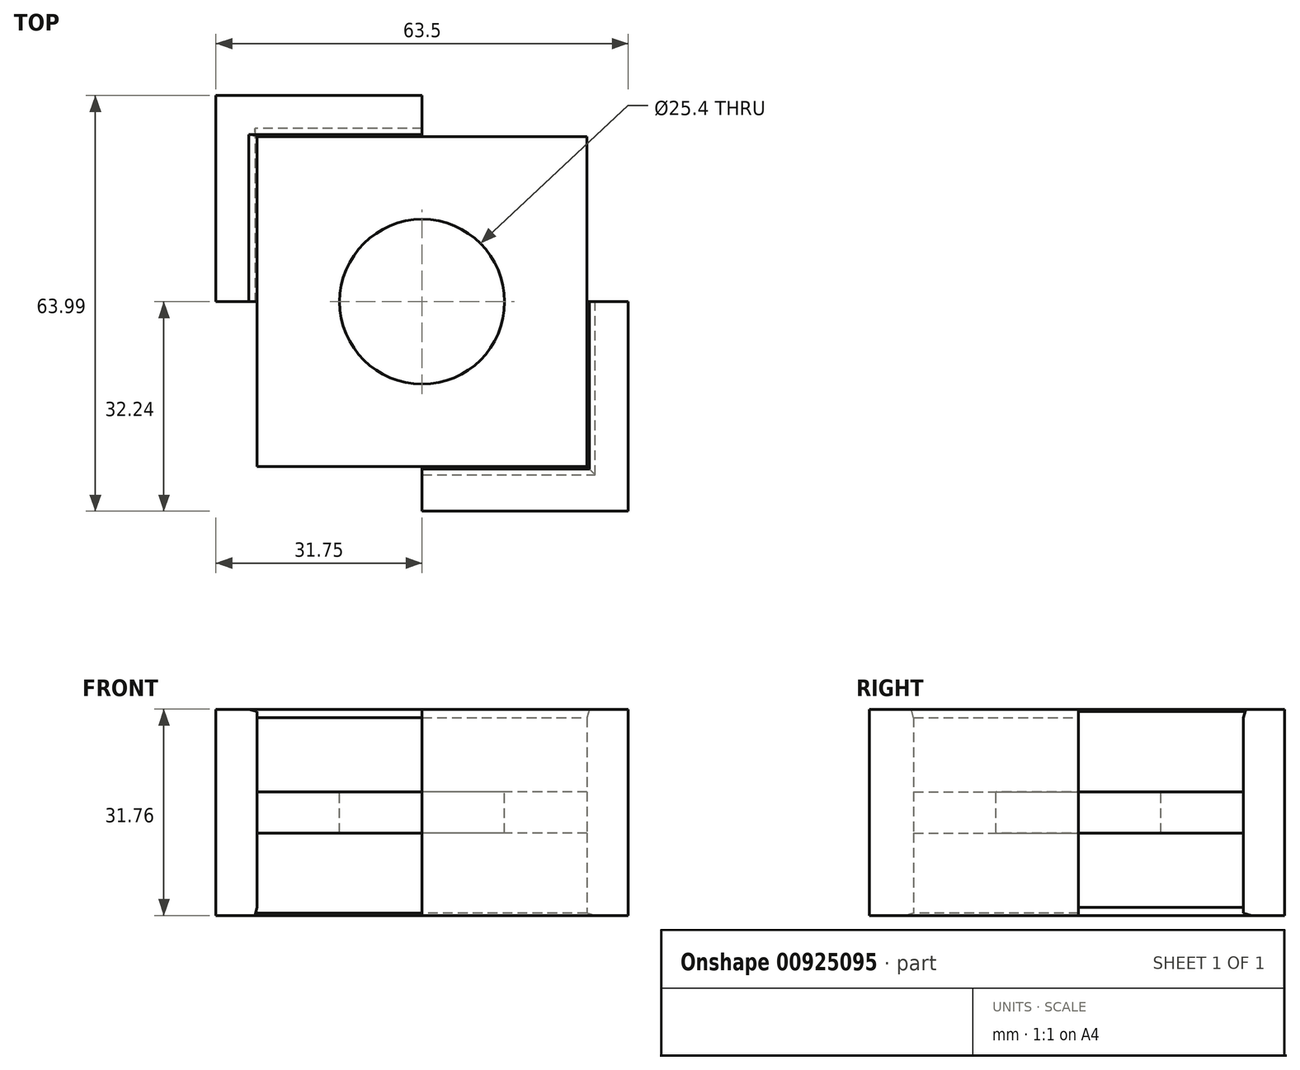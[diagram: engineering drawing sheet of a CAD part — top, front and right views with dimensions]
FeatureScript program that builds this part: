
annotation { "Feature Type Name" : "Feature", "Feature Type Description" : "" }
export const myFeature = defineFeature(function(context is Context, id is Id, definition is map)
    precondition{}
    {
        {
            var Q0;
            Q0=qCreatedBy(makeId("Top.planeOp"),FACE);
            var sketch = newSketch(context, id + "F0", { "sketchPlane" : qUnion([Q0])});
            skLineSegment(sketch, "E0.bottom", {"start": v(0, 0) * mm, "end": v(-50.8, 0) * mm});
            skLineSegment(sketch, "E0.top", {"start": v(0, 50.8) * mm, "end": v(-50.8, 50.8) * mm});
            skLineSegment(sketch, "E0.left", {"start": v(0, 0) * mm, "end": v(0, 50.8) * mm});
            skLineSegment(sketch, "E0.right", {"start": v(-50.8, 0) * mm, "end": v(-50.8, 50.8) * mm});
            skSolve(sketch);
        }
        {
            var Q0;
            Q0=qCreatedBy(makeId("Top.planeOp"),FACE);
            var sketch = newSketch(context, id + "F1", { "sketchPlane" : qUnion([Q0])});
            skLineSegment(sketch, "E1", {"start": v(0, 0) * mm, "end": v(0, 25.4) * mm});
            skLineSegment(sketch, "E2", {"start": v(0, 25.4) * mm, "end": v(6.35, 25.4) * mm});
            skLineSegment(sketch, "E3", {"start": v(6.35, 25.4) * mm, "end": v(6.35, -6.84) * mm});
            skLineSegment(sketch, "E4", {"start": v(6.35, -6.84) * mm, "end": v(-25.4, -6.84) * mm});
            skLineSegment(sketch, "E5", {"start": v(-25.4, -6.84) * mm, "end": v(-25.4, 0) * mm});
            skLineSegment(sketch, "E6", {"start": v(-25.4, 0) * mm, "end": v(0, 0) * mm});
            skSolve(sketch);
        }
        {
            var Q0;
            Q0=qCreatedBy(makeId("Top.planeOp"),FACE);
            var sketch = newSketch(context, id + "F2", { "sketchPlane" : qUnion([Q0])});
            skLineSegment(sketch, "E7.0", {"start": v(-25.4, 50.8) * mm, "end": v(-50.8, 50.8) * mm});
            skLineSegment(sketch, "E8.0", {"start": v(-50.8, 25.4) * mm, "end": v(-50.8, 50.8) * mm});
            skLineSegment(sketch, "E9", {"start": v(-25.4, 57.15) * mm, "end": v(-57.15, 57.15) * mm});
            skLineSegment(sketch, "E10", {"start": v(-57.15, 57.15) * mm, "end": v(-57.15, 25.4) * mm});
            skLineSegment(sketch, "E11", {"start": v(-57.15, 25.4) * mm, "end": v(-50.8, 25.4) * mm});
            skLineSegment(sketch, "E12", {"start": v(-25.4, 57.15) * mm, "end": v(-25.4, 50.8) * mm});
            skPoint(sketch, "E13.orphan", {"position": v(0, 50.8) * mm});
            skPoint(sketch, "E14.orphan", {"position": v(-50.8, 0) * mm});
            skSolve(sketch);
        }
        {
            var Q0;
            Q0 = qSketchRegion(id + "F0", true);
            extrude(context, id + "F3", {"entities" : qUnion([Q0]), "endBound" : BoundingType.SYMMETRIC, "depth" : 6.35 * mm, "offsetDistance" : 25.4 * mm});
        }
        {
            var Q0;
            Q0 = qSketchRegion(id + "F1", true);
            extrude(context, id + "F4", {"entities" : qUnion([Q0]), "operationType" : NewBodyOperationType.ADD, "endBound" : BoundingType.SYMMETRIC, "depth" : 31.75 * mm, "offsetDistance" : 25.4 * mm});
        }
        {
            var Q0;
            Q0 = qSketchRegion(id + "F2", true);
            extrude(context, id + "F5", {"entities" : qUnion([Q0]), "operationType" : NewBodyOperationType.ADD, "endBound" : BoundingType.SYMMETRIC, "depth" : 31.75 * mm, "offsetDistance" : 25.4 * mm});
        }
        {
            var Q0;
            Q0=makeQuery(id+"F4.opExtrude","CAP_EDGE",EDGE,{"disambiguationData":[OSD([sQuery(id+"F1.wireOp",EDGE,"E6")])],"isStart":false});
            var Q1;
            Q1=makeQuery(id+"F4.opExtrude","CAP_EDGE",EDGE,{"disambiguationData":[OSD([sQuery(id+"F1.wireOp",EDGE,"E1")])],"isStart":false});
            var Q2;
            Q2=makeQuery(id+"F5.opExtrude","CAP_EDGE",EDGE,{"disambiguationData":[OSD([sQuery(id+"F2.wireOp",EDGE,"E7.0")])],"isStart":false});
            var Q3;
            Q3=makeQuery(id+"F5.opExtrude","CAP_EDGE",EDGE,{"disambiguationData":[OSD([sQuery(id+"F2.wireOp",EDGE,"E8.0")])],"isStart":false});
            var Q4;
            Q4=makeQuery(id+"F4.opExtrude","CAP_EDGE",EDGE,{"disambiguationData":[OSD([sQuery(id+"F1.wireOp",EDGE,"E6")])],"isStart":true});
            var Q5;
            Q5=makeQuery(id+"F4.opExtrude","CAP_EDGE",EDGE,{"disambiguationData":[OSD([sQuery(id+"F1.wireOp",EDGE,"E1")])],"isStart":true});
            var Q6;
            Q6=makeQuery(id+"F5.opExtrude","CAP_EDGE",EDGE,{"disambiguationData":[OSD([sQuery(id+"F2.wireOp",EDGE,"E8.0")])],"isStart":true});
            var Q7;
            Q7=makeQuery(id+"F5.opExtrude","CAP_EDGE",EDGE,{"disambiguationData":[OSD([sQuery(id+"F2.wireOp",EDGE,"E7.0")])],"isStart":true});
            chamfer(context, id + "F6", {"entities" : qUnion([Q0, Q1, Q2, Q3, Q4, Q5, Q6, Q7]), "chamferType" : ChamferType.OFFSET_ANGLE, "width" : 1.27 * mm, "oppositeDirection" : false, "angle" : 15 * degree, "tangentPropagation" : true});
        }
        {
            var Q0;
            Q0=qCreatedBy(makeId("Top.planeOp"),FACE);
            var sketch = newSketch(context, id + "F7", { "sketchPlane" : qUnion([Q0])});
            skCircle(sketch, "E15", {"center": v(-25.4, 25.4) * mm, "radius": 12.7 * mm});
            skSolve(sketch);
        }
        {
            var Q0;
            Q0 = qSketchRegion(id + "F7", true);
            extrude(context, id + "F8", {"entities" : qUnion([Q0]), "operationType" : NewBodyOperationType.REMOVE, "endBound" : BoundingType.THROUGH_ALL, "oppositeDirection" : true, "depth" : 25.4 * mm, "offsetDistance" : 25.4 * mm, "hasSecondDirection" : true, "secondDirectionBound" : SecondDirectionBoundingType.THROUGH_ALL, "secondDirectionOppositeDirection" : false, "secondDirectionDepth" : 25.4 * mm});
        }
    });
